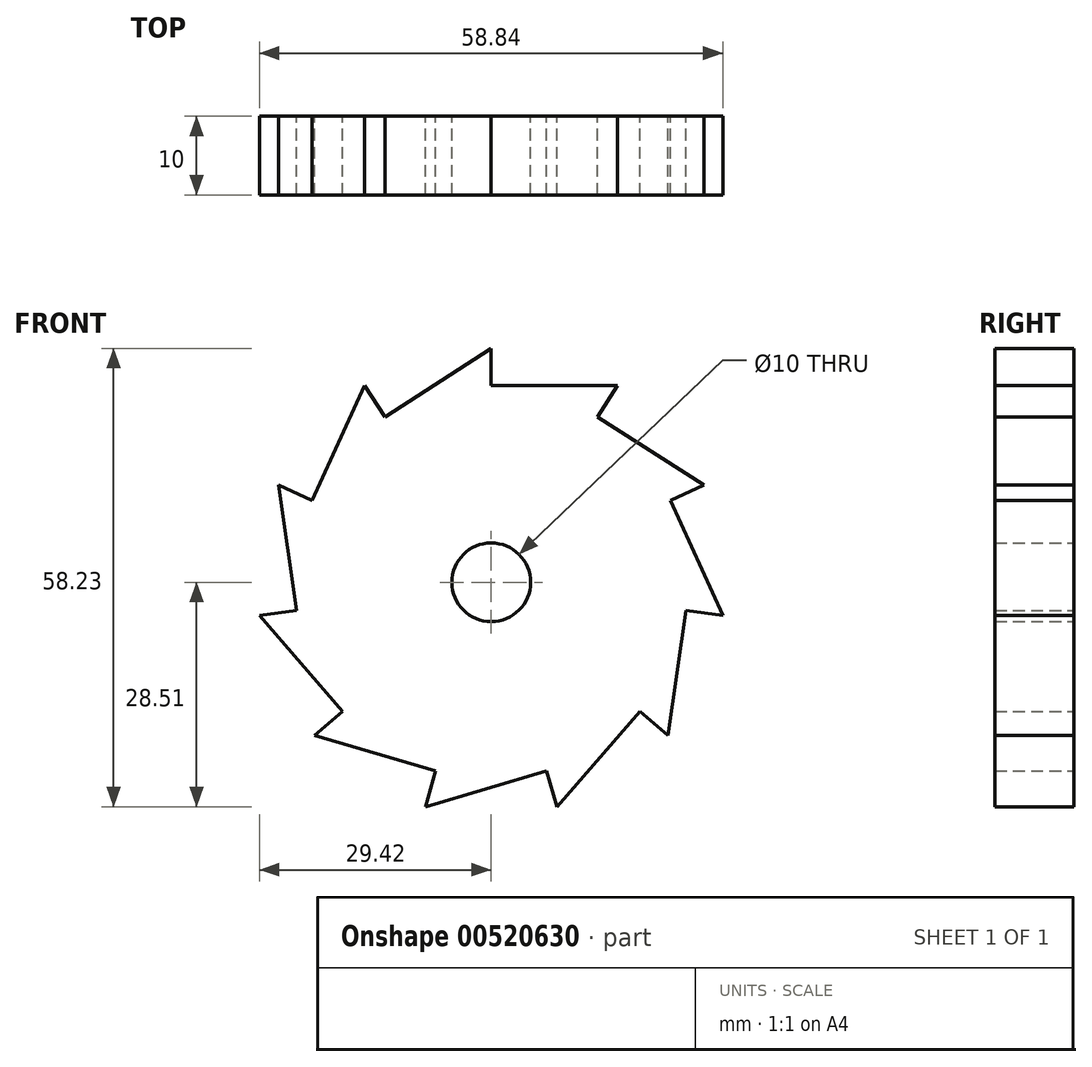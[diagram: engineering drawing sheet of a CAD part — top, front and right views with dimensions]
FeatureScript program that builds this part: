
annotation { "Feature Type Name" : "Feature", "Feature Type Description" : "" }
export const myFeature = defineFeature(function(context is Context, id is Id, definition is map)
    precondition{}
    {
        {
            var Q0;
            Q0=qCreatedBy(makeId("Front.planeOp"),FACE);
            var sketch = newSketch(context, id + "F0", { "sketchPlane" : qUnion([Q0])});
            skArc(sketch, "E0", {"start": v(-27.1, 12.86) * mm, "mid": v(-27.2, 12.66) * mm, "end": v(-27.29, 12.46) * mm});
            skLineSegment(sketch, "E1", {"start": v(0, 30) * mm, "end": v(0, 25) * mm});
            skLineSegment(sketch, "E2", {"start": v(0, 25) * mm, "end": v(16.58, 25) * mm});
            skLineSegment(sketch, "E3.1.0", {"start": v(-16.22, 25.24) * mm, "end": v(-13.52, 21.03) * mm});
            skLineSegment(sketch, "E3.1.1", {"start": v(-13.52, 21.03) * mm, "end": v(0.43, 30) * mm});
            skLineSegment(sketch, "E3.2.0", {"start": v(-27.29, 12.46) * mm, "end": v(-22.74, 10.39) * mm});
            skLineSegment(sketch, "E3.2.1", {"start": v(-22.74, 10.39) * mm, "end": v(-15.85, 25.47) * mm});
            skLineSegment(sketch, "E3.3.0", {"start": v(-29.7, -4.27) * mm, "end": v(-24.75, -3.56) * mm});
            skLineSegment(sketch, "E3.3.1", {"start": v(-24.75, -3.56) * mm, "end": v(-27.1, 12.86) * mm});
            skLineSegment(sketch, "E3.4.0", {"start": v(-22.67, -19.65) * mm, "end": v(-18.9, -16.37) * mm});
            skLineSegment(sketch, "E3.4.1", {"start": v(-18.9, -16.37) * mm, "end": v(-29.75, -3.84) * mm});
            skLineSegment(sketch, "E3.5.0", {"start": v(-8.45, -28.78) * mm, "end": v(-7.04, -23.99) * mm});
            skLineSegment(sketch, "E3.5.1", {"start": v(-7.04, -23.99) * mm, "end": v(-22.95, -19.32) * mm});
            skLineSegment(sketch, "E3.6.0", {"start": v(8.45, -28.78) * mm, "end": v(7.04, -23.99) * mm});
            skLineSegment(sketch, "E3.6.1", {"start": v(7.04, -23.99) * mm, "end": v(-8.87, -28.66) * mm});
            skLineSegment(sketch, "E3.7.0", {"start": v(22.67, -19.65) * mm, "end": v(18.9, -16.37) * mm});
            skLineSegment(sketch, "E3.7.1", {"start": v(18.9, -16.37) * mm, "end": v(8.03, -28.9) * mm});
            skLineSegment(sketch, "E3.8.0", {"start": v(29.7, -4.27) * mm, "end": v(24.75, -3.56) * mm});
            skLineSegment(sketch, "E3.8.1", {"start": v(24.75, -3.56) * mm, "end": v(22.39, -19.97) * mm});
            skLineSegment(sketch, "E3.9.0", {"start": v(27.29, 12.46) * mm, "end": v(22.74, 10.39) * mm});
            skLineSegment(sketch, "E3.9.1", {"start": v(22.74, 10.39) * mm, "end": v(29.63, -4.7) * mm});
            skLineSegment(sketch, "E3.10.0", {"start": v(16.22, 25.24) * mm, "end": v(13.52, 21.03) * mm});
            skLineSegment(sketch, "E3.10.1", {"start": v(13.52, 21.03) * mm, "end": v(27.47, 12.07) * mm});
            skArc(sketch, "E4.trimOffspring", {"start": v(-15.85, 25.47) * mm, "mid": v(-16.04, 25.35) * mm, "end": v(-16.22, 25.24) * mm});
            skArc(sketch, "E5.trimOffspring", {"start": v(0.43, 30) * mm, "mid": v(0.22, 30) * mm, "end": v(0, 30) * mm});
            skArc(sketch, "E6.trimOffspring", {"start": v(29.63, -4.7) * mm, "mid": v(29.66, -4.48) * mm, "end": v(29.7, -4.27) * mm});
            skArc(sketch, "E7.trimOffspring", {"start": v(22.39, -19.97) * mm, "mid": v(22.53, -19.8) * mm, "end": v(22.67, -19.65) * mm});
            skArc(sketch, "E8.trimOffspring", {"start": v(8.03, -28.9) * mm, "mid": v(8.24, -28.85) * mm, "end": v(8.45, -28.78) * mm});
            skArc(sketch, "E9.trimOffspring", {"start": v(-8.87, -28.66) * mm, "mid": v(-8.66, -28.72) * mm, "end": v(-8.45, -28.78) * mm});
            skArc(sketch, "E10.trimOffspring", {"start": v(-22.95, -19.32) * mm, "mid": v(-22.81, -19.48) * mm, "end": v(-22.67, -19.65) * mm});
            skArc(sketch, "E11.trimOffspring", {"start": v(-29.75, -3.84) * mm, "mid": v(-29.72, -4.05) * mm, "end": v(-29.7, -4.27) * mm});
            skCircle(sketch, "E12", {"center": v(0, 0) * mm, "radius": 5 * mm});
            skSolve(sketch);
        }
        {
            var Q0;
            Q0=makeQuery(id+"F0.imprint","IMPRINT",FACE,{"disambiguationData":[TD([[makeQuery(id+"F0.imprint","IMPRINT",EDGE,{"derivedFrom":sQuery(id+"F0.wireOp",EDGE,"E12")}),-1.0]])]});
            extrude(context, id + "F1", {"entities" : qUnion([Q0]), "depth" : 10 * mm, "offsetDistance" : 25 * mm});
        }
    });
